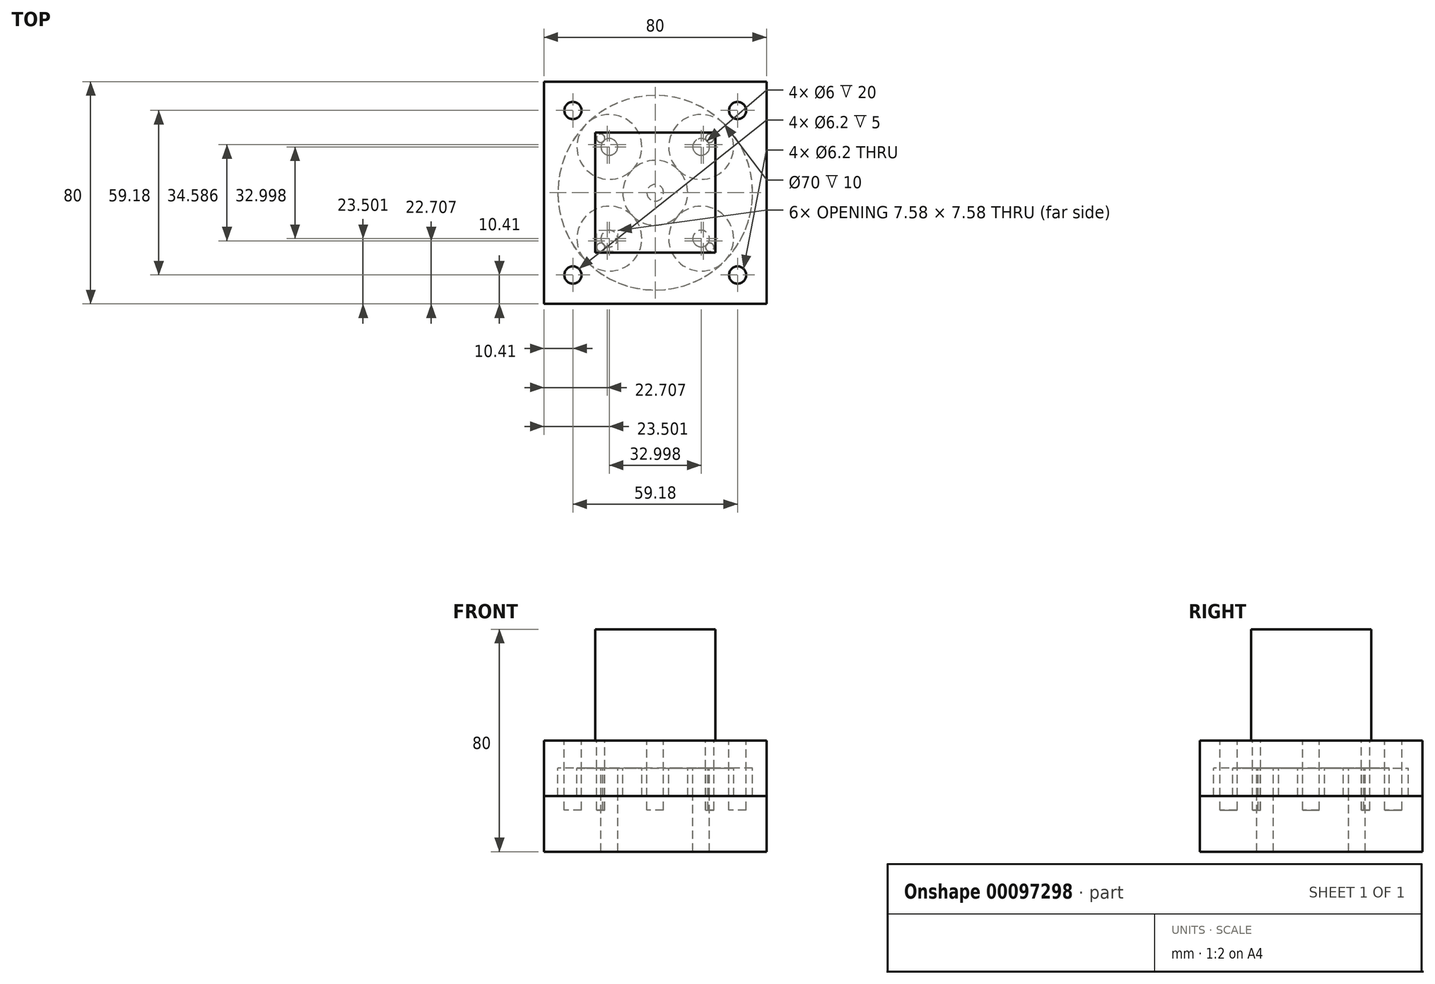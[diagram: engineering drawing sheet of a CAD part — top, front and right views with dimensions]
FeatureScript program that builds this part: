
annotation { "Feature Type Name" : "Feature", "Feature Type Description" : "" }
export const myFeature = defineFeature(function(context is Context, id is Id, definition is map)
    precondition{}
    {
        {
            var Q0;
            Q0=qCreatedBy(makeId("Top.planeOp"),FACE);
            var sketch = newSketch(context, id + "F0", { "sketchPlane" : qUnion([Q0])});
            skLineSegment(sketch, "E0.bottom", {"start": v(-40, -40) * mm, "end": v(40, -40) * mm});
            skLineSegment(sketch, "E0.top", {"start": v(-40, 40) * mm, "end": v(40, 40) * mm});
            skLineSegment(sketch, "E0.left", {"start": v(-40, -40) * mm, "end": v(-40, 40) * mm});
            skLineSegment(sketch, "E0.right", {"start": v(40, -40) * mm, "end": v(40, 40) * mm});
            skPoint(sketch, "E0.middle", {"position": v(0, 0) * mm});
            skLineSegment(sketch, "E1.0", {"start": v(-16.5, -16.5) * mm, "end": v(-16.5, 16.5) * mm, "construction": true});
            skLineSegment(sketch, "E1.1", {"start": v(-16.5, -16.5) * mm, "end": v(16.5, -16.5) * mm, "construction": true});
            skLineSegment(sketch, "E1.2", {"start": v(16.5, -16.5) * mm, "end": v(16.5, 16.5) * mm, "construction": true});
            skLineSegment(sketch, "E1.3", {"start": v(-16.5, 16.5) * mm, "end": v(16.5, 16.5) * mm, "construction": true});
            skCircle(sketch, "E2", {"center": v(-16.5, 16.5) * mm, "radius": 11.67 * mm});
            skCircle(sketch, "E3", {"center": v(-16.5, -16.5) * mm, "radius": 11.67 * mm});
            skCircle(sketch, "E4", {"center": v(16.5, -16.5) * mm, "radius": 11.67 * mm});
            skCircle(sketch, "E5", {"center": v(16.5, 16.5) * mm, "radius": 11.67 * mm});
            skCircle(sketch, "E6", {"center": v(0, 0) * mm, "radius": 11.67 * mm});
            skCircle(sketch, "E7", {"center": v(0, 0) * mm, "radius": 35 * mm});
            skCircle(sketch, "E8", {"center": v(-16.5, 16.5) * mm, "radius": 3 * mm});
            skCircle(sketch, "E9", {"center": v(-16.5, -16.5) * mm, "radius": 3 * mm});
            skCircle(sketch, "E10", {"center": v(16.5, -16.5) * mm, "radius": 3 * mm});
            skCircle(sketch, "E11", {"center": v(16.5, 16.5) * mm, "radius": 3 * mm});
            skCircle(sketch, "E12", {"center": v(0, 0) * mm, "radius": 3 * mm});
            skSolve(sketch);
        }
        {
            var Q0;
            Q0=makeQuery(id+"F0.imprint","IMPRINT",FACE,{"disambiguationData":[TD([[makeQuery(id+"F0.imprint","IMPRINT",EDGE,{"derivedFrom":sQuery(id+"F0.wireOp",EDGE,"E0.bottom")}),1.0]])]});
            var Q1;
            {var subQ0=sQuery(id+"F0.wireOp",EDGE,"E2");var subQ1=makeQuery(id+"F0.imprint","INTERSECT",VERTEX,{"derivedFrom":[subQ0,sQuery(id+"F0.wireOp",EDGE,"E6")]});Q1=makeQuery(id+"F0.imprint","IMPRINT",FACE,{"disambiguationData":[TD([[makeQuery(id+"F0.imprint","IMPRINT",EDGE,{"disambiguationData":[TD([[subQ1,1.0]])],"derivedFrom":subQ0}),1.0]])]});}
            var Q2;
            {var subQ0=sQuery(id+"F0.wireOp",EDGE,"E5");var subQ1=makeQuery(id+"F0.imprint","INTERSECT",VERTEX,{"derivedFrom":[subQ0,sQuery(id+"F0.wireOp",EDGE,"E6")]});Q2=makeQuery(id+"F0.imprint","IMPRINT",FACE,{"disambiguationData":[TD([[makeQuery(id+"F0.imprint","IMPRINT",EDGE,{"disambiguationData":[TD([[subQ1,1.0]])],"derivedFrom":subQ0}),1.0]])]});}
            var Q3;
            {var subQ0=sQuery(id+"F0.wireOp",EDGE,"E3");var subQ1=makeQuery(id+"F0.imprint","INTERSECT",VERTEX,{"derivedFrom":[subQ0,sQuery(id+"F0.wireOp",EDGE,"E6")]});Q3=makeQuery(id+"F0.imprint","IMPRINT",FACE,{"disambiguationData":[TD([[makeQuery(id+"F0.imprint","IMPRINT",EDGE,{"disambiguationData":[TD([[subQ1,-1.0]])],"derivedFrom":subQ0}),1.0]])]});}
            var Q4;
            {var subQ0=sQuery(id+"F0.wireOp",EDGE,"E4");var subQ1=makeQuery(id+"F0.imprint","INTERSECT",VERTEX,{"derivedFrom":[subQ0,sQuery(id+"F0.wireOp",EDGE,"E6")]});Q4=makeQuery(id+"F0.imprint","IMPRINT",FACE,{"disambiguationData":[TD([[makeQuery(id+"F0.imprint","IMPRINT",EDGE,{"disambiguationData":[TD([[subQ1,-1.0]])],"derivedFrom":subQ0}),1.0]])]});}
            var Q5;
            {var subQ0=sQuery(id+"F0.wireOp",EDGE,"E6");var subQ1=makeQuery(id+"F0.imprint","INTERSECT",VERTEX,{"derivedFrom":[sQuery(id+"F0.wireOp",EDGE,"E2"),subQ0]});Q5=makeQuery(id+"F0.imprint","IMPRINT",FACE,{"disambiguationData":[TD([[makeQuery(id+"F0.imprint","IMPRINT",EDGE,{"disambiguationData":[TD([[subQ1,1.0]])],"derivedFrom":subQ0}),1.0]])]});}
            extrude(context, id + "F1", {"entities" : qUnion([Q0, Q1, Q2, Q3, Q4, Q5]), "oppositeDirection" : true, "depth" : 10 * mm, "offsetDistance" : 25 * mm});
        }
        {
            var Q0;
            Q0=makeQuery(id+"F1.opExtrude","CAP_FACE",FACE,{"disambiguationData":[OSD([sQuery(id+"F0.wireOp",EDGE,"E0.bottom"),sQuery(id+"F0.wireOp",EDGE,"E0.top"),sQuery(id+"F0.wireOp",EDGE,"E0.left"),sQuery(id+"F0.wireOp",EDGE,"E0.right"),sQuery(id+"F0.wireOp",EDGE,"E7")])],"isStart":false});
            var sketch = newSketch(context, id + "F2", { "sketchPlane" : qUnion([Q0])});
            skLineSegment(sketch, "E13.0", {"start": v(-40, 40) * mm, "end": v(-40, -40) * mm});
            skLineSegment(sketch, "E14.0", {"start": v(-40, 40) * mm, "end": v(40, 40) * mm});
            skLineSegment(sketch, "E15.0", {"start": v(40, 40) * mm, "end": v(40, -40) * mm});
            skLineSegment(sketch, "E16.0", {"start": v(-40, -40) * mm, "end": v(40, -40) * mm});
            skCircle(sketch, "E17.0", {"center": v(-16.5, -16.5) * mm, "radius": 3 * mm});
            skCircle(sketch, "E18.0", {"center": v(-16.5, 16.5) * mm, "radius": 3 * mm});
            skCircle(sketch, "E19.0", {"center": v(16.5, 16.5) * mm, "radius": 3 * mm});
            skCircle(sketch, "E20.0", {"center": v(16.5, -16.5) * mm, "radius": 3 * mm});
            skSolve(sketch);
        }
        {
            var Q0;
            Q0 = qSketchRegion(id + "F2", true);
            extrude(context, id + "F3", {"entities" : qUnion([Q0]), "depth" : 20 * mm, "offsetDistance" : 25 * mm});
        }
        {
            var Q0;
            Q0=makeQuery(id+"F1.opExtrude","CAP_FACE",FACE,{"disambiguationData":[OSD([sQuery(id+"F0.wireOp",EDGE,"E0.bottom"),sQuery(id+"F0.wireOp",EDGE,"E0.top"),sQuery(id+"F0.wireOp",EDGE,"E0.left"),sQuery(id+"F0.wireOp",EDGE,"E0.right"),sQuery(id+"F0.wireOp",EDGE,"E7")])],"isStart":true});
            var sketch = newSketch(context, id + "F4", { "sketchPlane" : qUnion([Q0])});
            skLineSegment(sketch, "E21.0", {"start": v(-40, 40) * mm, "end": v(40, 40) * mm});
            skLineSegment(sketch, "E21.1", {"start": v(-40, -40) * mm, "end": v(40, -40) * mm});
            skLineSegment(sketch, "E21.2", {"start": v(40, -40) * mm, "end": v(40, 40) * mm});
            skLineSegment(sketch, "E21.3", {"start": v(-40, -40) * mm, "end": v(-40, 40) * mm});
            skSolve(sketch);
        }
        {
            var Q0;
            Q0 = qSketchRegion(id + "F4", true);
            extrude(context, id + "F5", {"entities" : qUnion([Q0]), "operationType" : NewBodyOperationType.ADD, "depth" : 10 * mm, "offsetDistance" : 25 * mm});
        }
        {
            var Q0;
            Q0=makeQuery(id+"F5.opExtrude","CAP_FACE",FACE,{"disambiguationData":[OSD([sQuery(id+"F4.wireOp",EDGE,"E21.0"),sQuery(id+"F4.wireOp",EDGE,"E21.1"),sQuery(id+"F4.wireOp",EDGE,"E21.2"),sQuery(id+"F4.wireOp",EDGE,"E21.3")])],"isStart":false});
            var sketch = newSketch(context, id + "F6", { "sketchPlane" : qUnion([Q0])});
            skLineSegment(sketch, "E22.bottom", {"start": v(21.6, -21.59) * mm, "end": v(-21.6, -21.6) * mm});
            skLineSegment(sketch, "E22.top", {"start": v(21.6, 21.6) * mm, "end": v(-21.6, 21.6) * mm});
            skLineSegment(sketch, "E22.left", {"start": v(21.6, -21.6) * mm, "end": v(21.6, 21.6) * mm});
            skLineSegment(sketch, "E22.right", {"start": v(-21.6, -21.6) * mm, "end": v(-21.6, 21.59) * mm});
            skPoint(sketch, "E22.middle", {"position": v(0, 0) * mm});
            skLineSegment(sketch, "E23.0", {"start": v(19.59, -19.59) * mm, "end": v(-19.6, -19.6) * mm, "construction": true});
            skLineSegment(sketch, "E23.1", {"start": v(19.59, -19.59) * mm, "end": v(19.59, 19.6) * mm, "construction": true});
            skLineSegment(sketch, "E23.2", {"start": v(19.59, 19.6) * mm, "end": v(-19.6, 19.59) * mm, "construction": true});
            skLineSegment(sketch, "E23.3", {"start": v(-19.6, -19.6) * mm, "end": v(-19.6, 19.59) * mm, "construction": true});
            skCircle(sketch, "E24", {"center": v(-19.6, -19.6) * mm, "radius": 1.5 * mm});
            skCircle(sketch, "E25", {"center": v(-19.6, 19.59) * mm, "radius": 1.5 * mm});
            skCircle(sketch, "E26", {"center": v(19.59, -19.59) * mm, "radius": 1.5 * mm});
            skCircle(sketch, "E27", {"center": v(19.59, 19.6) * mm, "radius": 1.5 * mm});
            skCircle(sketch, "E28", {"center": v(0, 0) * mm, "radius": 3 * mm});
            skLineSegment(sketch, "E29.0", {"start": v(29.59, -29.6) * mm, "end": v(-29.6, -29.6) * mm, "construction": true});
            skLineSegment(sketch, "E29.1", {"start": v(29.59, -29.6) * mm, "end": v(29.59, 29.6) * mm, "construction": true});
            skLineSegment(sketch, "E29.2", {"start": v(29.59, 29.6) * mm, "end": v(-29.6, 29.6) * mm, "construction": true});
            skLineSegment(sketch, "E29.3", {"start": v(-29.6, -29.6) * mm, "end": v(-29.6, 29.6) * mm, "construction": true});
            skCircle(sketch, "E30", {"center": v(-29.6, -29.6) * mm, "radius": 3.1 * mm});
            skCircle(sketch, "E31", {"center": v(29.59, -29.6) * mm, "radius": 3.1 * mm});
            skCircle(sketch, "E32", {"center": v(29.59, 29.6) * mm, "radius": 3.1 * mm});
            skCircle(sketch, "E33", {"center": v(-29.6, 29.6) * mm, "radius": 3.1 * mm});
            skSolve(sketch);
        }
        {
            var Q0;
            Q0=makeQuery(id+"F6.imprint","IMPRINT",FACE,{"disambiguationData":[TD([[makeQuery(id+"F6.imprint","IMPRINT",EDGE,{"derivedFrom":sQuery(id+"F6.wireOp",EDGE,"E26")}),1.0]])]});
            var Q1;
            Q1=makeQuery(id+"F6.imprint","IMPRINT",FACE,{"disambiguationData":[TD([[makeQuery(id+"F6.imprint","IMPRINT",EDGE,{"derivedFrom":sQuery(id+"F6.wireOp",EDGE,"E24")}),1.0]])]});
            var Q2;
            Q2=makeQuery(id+"F6.imprint","IMPRINT",FACE,{"disambiguationData":[TD([[makeQuery(id+"F6.imprint","IMPRINT",EDGE,{"derivedFrom":sQuery(id+"F6.wireOp",EDGE,"E25")}),1.0]])]});
            var Q3;
            Q3=makeQuery(id+"F6.imprint","IMPRINT",FACE,{"disambiguationData":[TD([[makeQuery(id+"F6.imprint","IMPRINT",EDGE,{"derivedFrom":sQuery(id+"F6.wireOp",EDGE,"E27")}),1.0]])]});
            var Q4;
            Q4=makeQuery(id+"F6.imprint","IMPRINT",FACE,{"disambiguationData":[TD([[makeQuery(id+"F6.imprint","IMPRINT",EDGE,{"derivedFrom":sQuery(id+"F6.wireOp",EDGE,"E28")}),1.0]])]});
            var Q5;
            Q5=makeQuery(id+"F6.imprint","IMPRINT",FACE,{"disambiguationData":[TD([[makeQuery(id+"F6.imprint","IMPRINT",EDGE,{"derivedFrom":sQuery(id+"F6.wireOp",EDGE,"E22.bottom")}),-1.0]])]});
            extrude(context, id + "F7", {"entities" : qUnion([Q0, Q1, Q2, Q3, Q4, Q5]), "depth" : 40 * mm, "offsetDistance" : 25 * mm});
        }
        {
            var Q0;
            Q0=makeQuery(id+"F6.imprint","IMPRINT",FACE,{"disambiguationData":[TD([[makeQuery(id+"F6.imprint","IMPRINT",EDGE,{"derivedFrom":sQuery(id+"F6.wireOp",EDGE,"E26")}),1.0]])]});
            var Q1;
            Q1=makeQuery(id+"F6.imprint","IMPRINT",FACE,{"disambiguationData":[TD([[makeQuery(id+"F6.imprint","IMPRINT",EDGE,{"derivedFrom":sQuery(id+"F6.wireOp",EDGE,"E24")}),1.0]])]});
            var Q2;
            Q2=makeQuery(id+"F6.imprint","IMPRINT",FACE,{"disambiguationData":[TD([[makeQuery(id+"F6.imprint","IMPRINT",EDGE,{"derivedFrom":sQuery(id+"F6.wireOp",EDGE,"E25")}),1.0]])]});
            var Q3;
            Q3=makeQuery(id+"F6.imprint","IMPRINT",FACE,{"disambiguationData":[TD([[makeQuery(id+"F6.imprint","IMPRINT",EDGE,{"derivedFrom":sQuery(id+"F6.wireOp",EDGE,"E27")}),1.0]])]});
            var Q4;
            Q4=makeQuery(id+"F6.imprint","IMPRINT",FACE,{"disambiguationData":[TD([[makeQuery(id+"F6.imprint","IMPRINT",EDGE,{"derivedFrom":sQuery(id+"F6.wireOp",EDGE,"E28")}),1.0]])]});
            var Q5;
            Q5=makeQuery(id+"F6.imprint","IMPRINT",FACE,{"disambiguationData":[TD([[makeQuery(id+"F6.imprint","IMPRINT",EDGE,{"derivedFrom":sQuery(id+"F6.wireOp",EDGE,"E30")}),1.0]])]});
            var Q6;
            Q6=makeQuery(id+"F6.imprint","IMPRINT",FACE,{"disambiguationData":[TD([[makeQuery(id+"F6.imprint","IMPRINT",EDGE,{"derivedFrom":sQuery(id+"F6.wireOp",EDGE,"E31")}),1.0]])]});
            var Q7;
            Q7=makeQuery(id+"F6.imprint","IMPRINT",FACE,{"disambiguationData":[TD([[makeQuery(id+"F6.imprint","IMPRINT",EDGE,{"derivedFrom":sQuery(id+"F6.wireOp",EDGE,"E33")}),1.0]])]});
            var Q8;
            Q8=makeQuery(id+"F6.imprint","IMPRINT",FACE,{"disambiguationData":[TD([[makeQuery(id+"F6.imprint","IMPRINT",EDGE,{"derivedFrom":sQuery(id+"F6.wireOp",EDGE,"E32")}),1.0]])]});
            extrude(context, id + "F8", {"entities" : qUnion([Q0, Q1, Q2, Q3, Q4, Q5, Q6, Q7, Q8]), "operationType" : NewBodyOperationType.REMOVE, "oppositeDirection" : true, "depth" : 25 * mm, "offsetDistance" : 25 * mm});
        }
    });
